# Revit family: Thorn BETA2
name_source: partatom
category: Leuchten
revit_build: Autodesk Revit 2016 (Build: 20150714_1515(x64)
units: mm (PartAtom-declared; Revit-internal decimal feet)

## family parameters
Basisbauteil = Fläche
Beim Laden mit Abzugskörper schneiden = Nein
Bemaßung runder Anschluss = Durchmesser verwenden
Gemeinsam genutzt = Nein
Lichtquelle = Ja
OmniClass-Nummer = 23.80.70.11
OmniClass-Titel = Luminaries for Internal Lighting
Raumberechnungspunkt = Nein
Teiletyp = Normal

## types (7) — shared parameters
Baugruppenkennzeichen = D5020200
Beschreibung = Recessed LED luminaire
Body = Thorn_Metal_White
Cover = Thorn_PMMA_Opaque
Emissionsform beim Rendern sichtbar = Nein
Farbfilter = 16777215
Farbtemperaturverschiebung bei Dämpfen der Lampe = <Keine Auswahl>
Height = 14 mm  [stored 0.0459318 ft]
Hersteller = Thorn Lighting
Lampe = LED
Neigungswinkel = -90.00°
Voltage = 230 V
zero-valued in all types: Vorgabe-Ansicht

## per-type parameters (varying)
| type | Datei für fotometrisches Netz | Length | Modell | Scheinlast | URL | Von Breite des Rechtecks ausssenden | Von Länge des Rechtecks aussenden | Width |
| BETA 2 LED3000 300x1200 | TL_BET2_RLO840.IES | 1196 mm | 96631473 | 28 VA | www.thornlighting.com/96631473 | 1146 mm | 246 mm | 296 mm |
| BETA 2 LED3800 300x1200 | TL_BET2_RHO840.IES | 1196 mm | 96631466 | 36 VA | www.thornlighting.com/96631466 | 1146 mm | 246 mm | 296 mm |
| BETA 2 LED3000 M600Q | TL_BET2_QLO840.IES | 596 mm  [stored 1.95538 ft] | 96631455 | 25 VA | www.thornlighting.com/96631455 | 546 mm  [stored 1.79134 ft] | 546 mm  [stored 1.79134 ft] | 596 mm  [stored 1.95538 ft] |
| BETA 2 LED3000 M625Q | TL_BET2_QLO840.IES | 621 mm | 96631459 | 25 VA | www.thornlighting.com/96631459 | 571 mm | 571 mm | 621 mm |
| BETA 2 LED3800 M600Q | TL_BET2_QLO840.IES | 596 mm  [stored 1.95538 ft] | 96631444 | 33 VA | www.thornlighting.com/96631444 | 546 mm  [stored 1.79134 ft] | 546 mm  [stored 1.79134 ft] | 596 mm  [stored 1.95538 ft] |
| BETA 2 LED3800 M625Q | TL_BET2_QLO840.IES | 621 mm | 96631448 | 33 VA | www.thornlighting.com/96631448 | 571 mm | 571 mm | 621 mm |
| BETA 2 LED3000 E3D M600Q | 96631463_(STD).IES | 596 mm  [stored 1.95538 ft] | 96631463 | 25 VA | www.thornlighting.com/96631463 | 546 mm  [stored 1.79134 ft] | 546 mm  [stored 1.79134 ft] | 596 mm  [stored 1.95538 ft] |

note: [stored X ft] marks values corroborated as IEEE doubles in the binary element streams (Revit-internal decimal feet)

## geometry (parser evidence)
native form markers: Sweep x3
no freeform markers — native parametric forms only
